# Revit family: 455075551_Griferia_LavaplatosSencillo_Residencial_Nogal
name_source: partatom
category: Plumbing Fixtures
units: mm (PartAtom-declared; Revit-internal decimal feet)

## family parameters
Cut with Voids When Loaded = No
Host = Face
OmniClass Number = 23.31.11.00
OmniClass Title = Faucets
Part Type = Normal
Room Calculation Point = No
Round Connector Dimension = Use Diameter
Shared = No

## types (1)
- 455075551_Griferia_LavaplatosSencillo_Residencial_Nogal
    Alto = 345 mm
    Ancho = 92 mm
    Capacidad de flujo = A 60 psi: 7.0 L/min.
    Default Elevation = 0 mm  [stored 0 ft]
    Description = La griferia de cocinas Nogal ha sido diselada para trabajar en perfecta armonía con el espacio; inspirada en las necesidades del consumidor latinoamericano dando como resultado un producto robusto y funcional. Su pico giratorio le permite al usuario tomar ventaja del área del lavaplatos. Ideal para instalaciones donde no se necesita mezclar agua fría y caliente. Incorpora un sistema aireador que genera un chorro de agua espumoso,agradable al tacto.
    Dimensiones generales del producto = 340 x 92 x 160 mm.
    Diámetro abasto = 13 mm
    Garantía = 30 años Grival - 2 años Cromado.
    Manufacturer = Corona.
    Material = Corona_Cromado
    Material 2 = Corona_Acero inoxidable
    Model = 455075551_Griferia_LavaplatosSencillo_Residencial_Nogal
    Normatividad = NTC 1644.
    Peso  Bruto = 720 gr. / 1.58 lb.
    Peso neto = 640 gr./ / 1.41 lb.
    Presión máxima recomendada = 20 psi (138 kPa).
    Presión mínima recomendada = 125 psi (862 kPa).
    Profundidad = 248 mm
    Recubrimientos = Resiste a la corrosión, pelado y decoloración por agua. Recubrimientos no tóxicos. Producto para uso doméstico.
    Temperaturas máxima de trabajo = 71° C.
    Temperaturas mínima de trabajo = 5° C.
    Vida útil = (Unidad): 500000 ciclos - (Giratorio): 50000 ciclos.

note: [stored X ft] marks values corroborated as IEEE doubles in the binary element streams (Revit-internal decimal feet)

## geometry (parser evidence)
native form markers: Sweep x9
no freeform markers — native parametric forms only
